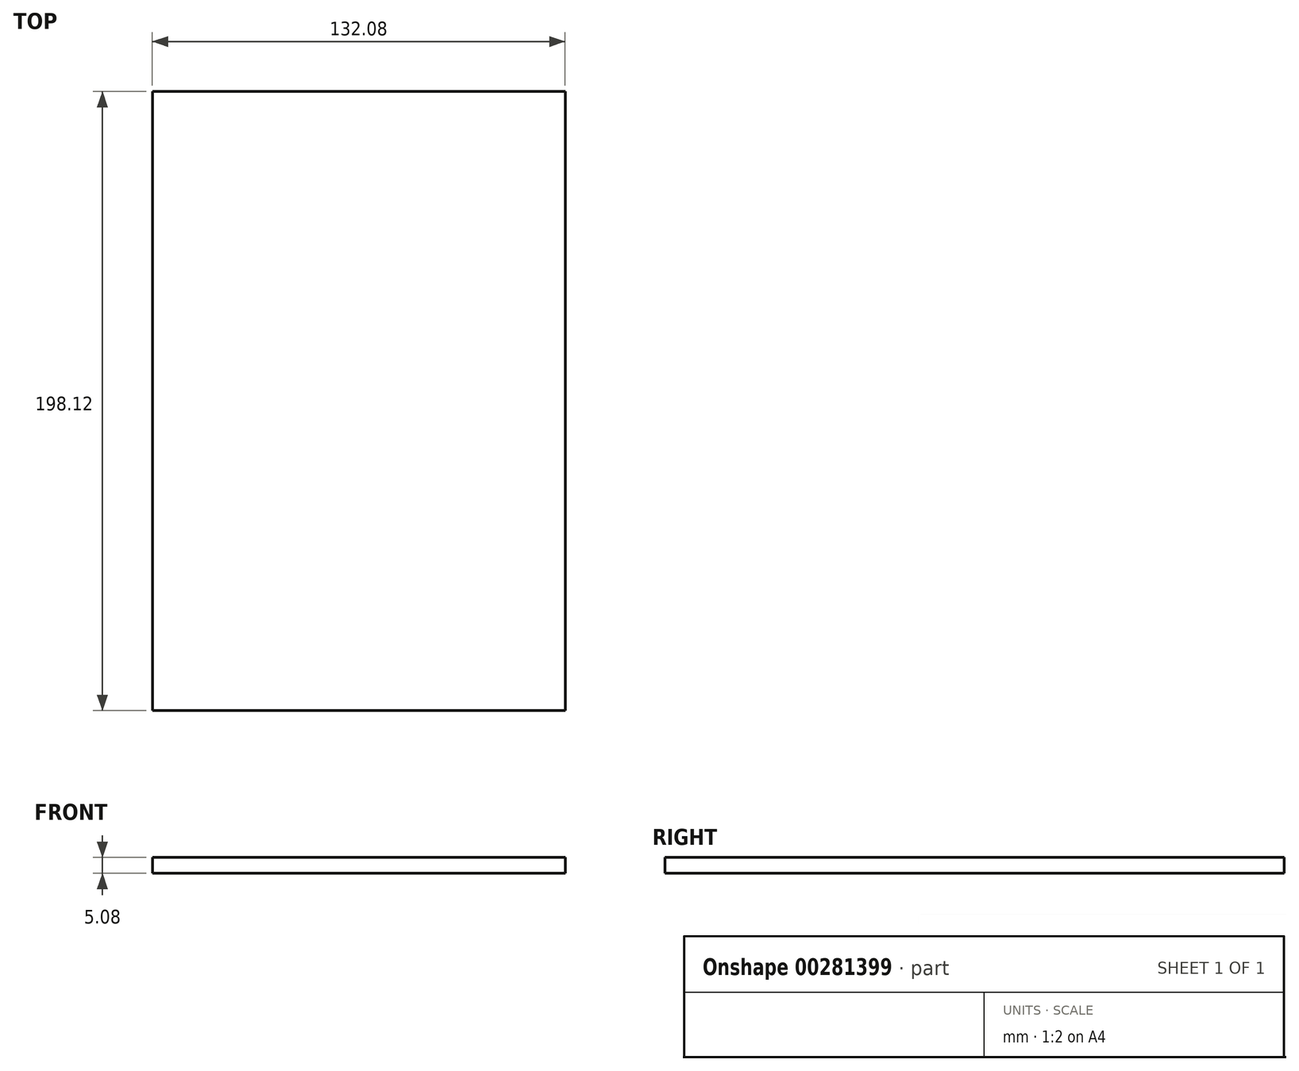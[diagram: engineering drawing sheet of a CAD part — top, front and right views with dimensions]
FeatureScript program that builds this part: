
annotation { "Feature Type Name" : "Feature", "Feature Type Description" : "" }
export const myFeature = defineFeature(function(context is Context, id is Id, definition is map)
    precondition{}
    {
        {
            var Q0;
            Q0=qCreatedBy(makeId("Top.planeOp"),FACE);
            var sketch = newSketch(context, id + "F0", { "sketchPlane" : qUnion([Q0])});
            skLineSegment(sketch, "E0.bottom", {"start": v(-78.89, 97.86) * mm, "end": v(53.2, 97.86) * mm});
            skLineSegment(sketch, "E0.top", {"start": v(-78.89, -100.26) * mm, "end": v(53.2, -100.26) * mm});
            skLineSegment(sketch, "E0.left", {"start": v(-78.89, 97.86) * mm, "end": v(-78.89, -100.26) * mm});
            skLineSegment(sketch, "E0.right", {"start": v(53.2, 97.86) * mm, "end": v(53.2, -100.26) * mm});
            skSolve(sketch);
        }
        {
            var Q0;
            Q0=makeQuery(id+"F0.imprint","IMPRINT",FACE,{"disambiguationData":[TD([[makeQuery(id+"F0.imprint","IMPRINT",EDGE,{"derivedFrom":sQuery(id+"F0.wireOp",EDGE,"E0.bottom")}),-1.0]])]});
            extrude(context, id + "F1", {"entities" : qUnion([Q0]), "depth" : 5.08 * mm});
        }
    });
